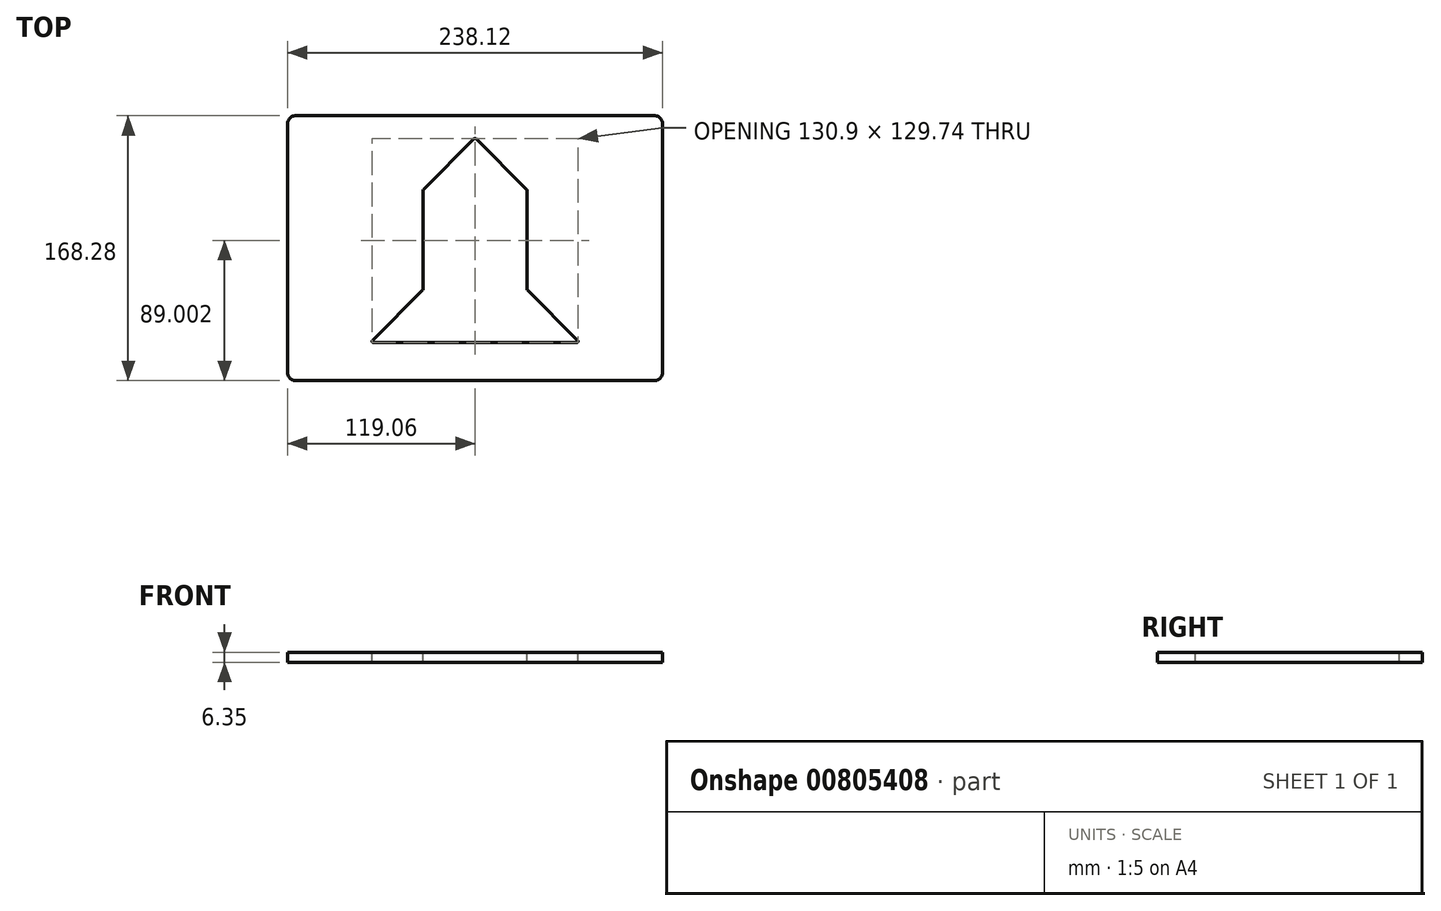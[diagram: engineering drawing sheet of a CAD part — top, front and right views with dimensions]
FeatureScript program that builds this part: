
annotation { "Feature Type Name" : "Feature", "Feature Type Description" : "" }
export const myFeature = defineFeature(function(context is Context, id is Id, definition is map)
    precondition{}
    {
        {
            var Q0;
            Q0=qCreatedBy(makeId("Top.planeOp"),FACE);
            var sketch = newSketch(context, id + "F0", { "sketchPlane" : qUnion([Q0])});
            skLineSegment(sketch, "E0.bottom", {"start": v(119.06, 84.14) * mm, "end": v(-119.06, 84.14) * mm});
            skLineSegment(sketch, "E0.top", {"start": v(119.06, -84.14) * mm, "end": v(-119.06, -84.14) * mm});
            skLineSegment(sketch, "E0.left", {"start": v(119.06, 84.14) * mm, "end": v(119.06, -84.14) * mm});
            skLineSegment(sketch, "E0.right", {"start": v(-119.06, 84.14) * mm, "end": v(-119.06, -84.14) * mm});
            skPoint(sketch, "E0.middle", {"position": v(0, 0) * mm});
            skSolve(sketch);
        }
        {
            var Q0;
            Q0 = qSketchRegion(id + "F0", true);
            extrude(context, id + "F1", {"entities" : qUnion([Q0]), "depth" : 6.35 * mm, "offsetDistance" : 25.4 * mm});
        }
        {
            var Q0;
            Q0=makeQuery(id+"F1.opExtrude","SWEPT_EDGE",EDGE,{"disambiguationData":[OSD([sQuery(id+"F0.wireOp",EDGE,"E0.bottom"),sQuery(id+"F0.wireOp",EDGE,"E0.right")])]});
            var Q1;
            Q1=makeQuery(id+"F1.opExtrude","SWEPT_EDGE",EDGE,{"disambiguationData":[OSD([sQuery(id+"F0.wireOp",EDGE,"E0.bottom"),sQuery(id+"F0.wireOp",EDGE,"E0.left")])]});
            var Q2;
            Q2=makeQuery(id+"F1.opExtrude","SWEPT_EDGE",EDGE,{"disambiguationData":[OSD([sQuery(id+"F0.wireOp",EDGE,"E0.top"),sQuery(id+"F0.wireOp",EDGE,"E0.right")])]});
            var Q3;
            Q3=makeQuery(id+"F1.opExtrude","SWEPT_EDGE",EDGE,{"disambiguationData":[OSD([sQuery(id+"F0.wireOp",EDGE,"E0.top"),sQuery(id+"F0.wireOp",EDGE,"E0.left")])]});
            fillet(context, id + "F2", {"entities" : qUnion([Q0, Q1, Q2, Q3]), "radius" : 5.08 * mm, "tangentPropagation" : true, "allowEdgeOverflow" : false});
        }
        {
            var Q0;
            Q0=makeQuery(id+"F1.opExtrude","CAP_FACE",FACE,{"disambiguationData":[OSD([sQuery(id+"F0.wireOp",EDGE,"E0.bottom"),sQuery(id+"F0.wireOp",EDGE,"E0.top"),sQuery(id+"F0.wireOp",EDGE,"E0.left"),sQuery(id+"F0.wireOp",EDGE,"E0.right")])],"isStart":false});
            var sketch = newSketch(context, id + "F3", { "sketchPlane" : qUnion([Q0])});
            skLineSegment(sketch, "E1", {"start": v(0, -58.74) * mm, "end": v(-63.5, -58.74) * mm});
            skLineSegment(sketch, "E2", {"start": v(-63.5, -58.74) * mm, "end": v(-31.75, -26.99) * mm});
            skLineSegment(sketch, "E3", {"start": v(-31.75, -26.99) * mm, "end": v(-31.75, 36.51) * mm});
            skLineSegment(sketch, "E4", {"start": v(-31.75, 36.51) * mm, "end": v(0, 68.26) * mm});
            skLineSegment(sketch, "E5.MirrorCS", {"start": v(31.75, 36.51) * mm, "end": v(0, 68.26) * mm});
            skLineSegment(sketch, "E6.MirrorCS", {"start": v(31.75, -26.99) * mm, "end": v(31.75, 36.51) * mm});
            skLineSegment(sketch, "E7.MirrorCS", {"start": v(63.5, -58.74) * mm, "end": v(31.75, -26.99) * mm});
            skLineSegment(sketch, "E8.MirrorCS", {"start": v(0, -58.74) * mm, "end": v(63.5, -58.74) * mm});
            skSolve(sketch);
        }
        {
            var Q0;
            Q0 = qSketchRegion(id + "F3", true);
            extrude(context, id + "F4", {"entities" : qUnion([Q0]), "operationType" : NewBodyOperationType.REMOVE, "oppositeDirection" : true, "depth" : 25.4 * mm, "offsetDistance" : 25.4 * mm});
        }
        {
            var Q0;
            Q0 = qSketchRegion(id + "F3", true);
            extrude(context, id + "F5", {"entities" : qUnion([Q0]), "operationType" : NewBodyOperationType.REMOVE, "endBound" : BoundingType.THROUGH_ALL, "oppositeDirection" : true, "depth" : 25.4 * mm, "offsetDistance" : 25.4 * mm});
        }
        {
            var Q0;
            Q0=makeQuery(id+"F1.opExtrude","CAP_FACE",FACE,{"disambiguationData":[OSD([sQuery(id+"F0.wireOp",EDGE,"E0.bottom"),sQuery(id+"F0.wireOp",EDGE,"E0.top"),sQuery(id+"F0.wireOp",EDGE,"E0.left"),sQuery(id+"F0.wireOp",EDGE,"E0.right")])],"isStart":false});
            var sketch = newSketch(context, id + "F6", { "sketchPlane" : qUnion([Q0])});
            skLineSegment(sketch, "E9.0", {"start": v(-33.02, -26.14) * mm, "end": v(-33.02, 36.71) * mm});
            skLineSegment(sketch, "E9.1", {"start": v(-65.22, -58.66) * mm, "end": v(-33.25, -26.7) * mm});
            skLineSegment(sketch, "E9.2", {"start": v(32.79, 37.27) * mm, "end": v(0.56, 69.5) * mm});
            skLineSegment(sketch, "E9.3", {"start": v(33.02, -26.14) * mm, "end": v(33.02, 36.71) * mm});
            skLineSegment(sketch, "E9.4", {"start": v(65.22, -58.66) * mm, "end": v(33.25, -26.7) * mm});
            skLineSegment(sketch, "E9.5", {"start": v(-32.79, 37.27) * mm, "end": v(-0.56, 69.5) * mm});
            skLineSegment(sketch, "E9.6", {"start": v(64.67, -60) * mm, "end": v(-64.67, -60) * mm});
            skPoint(sketch, "E10.visualSharp", {"position": v(0, 70.06) * mm});
            skArc(sketch, "E10.filletArc", {"start": v(0.56, 69.5) * mm, "mid": v(0, 69.73) * mm, "end": v(-0.56, 69.5) * mm});
            skPoint(sketch, "E11.visualSharp", {"position": v(33.02, 37.04) * mm});
            skArc(sketch, "E11.filletArc", {"start": v(33.02, 36.71) * mm, "mid": v(32.96, 37.01) * mm, "end": v(32.79, 37.27) * mm});
            skPoint(sketch, "E12.visualSharp", {"position": v(33.02, -26.46) * mm});
            skArc(sketch, "E12.filletArc", {"start": v(33.02, -26.14) * mm, "mid": v(33.08, -26.44) * mm, "end": v(33.25, -26.7) * mm});
            skPoint(sketch, "E13.visualSharp", {"position": v(66.57, -60) * mm});
            skArc(sketch, "E13.filletArc", {"start": v(64.67, -60) * mm, "mid": v(65.4, -59.52) * mm, "end": v(65.22, -58.66) * mm});
            skPoint(sketch, "E14.visualSharp", {"position": v(-66.57, -60) * mm});
            skArc(sketch, "E14.filletArc", {"start": v(-65.22, -58.66) * mm, "mid": v(-65.4, -59.52) * mm, "end": v(-64.67, -60) * mm});
            skPoint(sketch, "E15.visualSharp", {"position": v(-33.02, -26.46) * mm});
            skArc(sketch, "E15.filletArc", {"start": v(-33.25, -26.7) * mm, "mid": v(-33.08, -26.44) * mm, "end": v(-33.02, -26.14) * mm});
            skPoint(sketch, "E16.visualSharp", {"position": v(-33.02, 37.04) * mm});
            skArc(sketch, "E16.filletArc", {"start": v(-32.79, 37.27) * mm, "mid": v(-32.96, 37.01) * mm, "end": v(-33.02, 36.71) * mm});
            skSolve(sketch);
        }
        {
            var Q0;
            Q0 = qSketchRegion(id + "F6", true);
            extrude(context, id + "F7", {"entities" : qUnion([Q0]), "operationType" : NewBodyOperationType.REMOVE, "endBound" : BoundingType.THROUGH_ALL, "oppositeDirection" : true, "depth" : 25.4 * mm, "offsetDistance" : 25.4 * mm});
        }
    });
